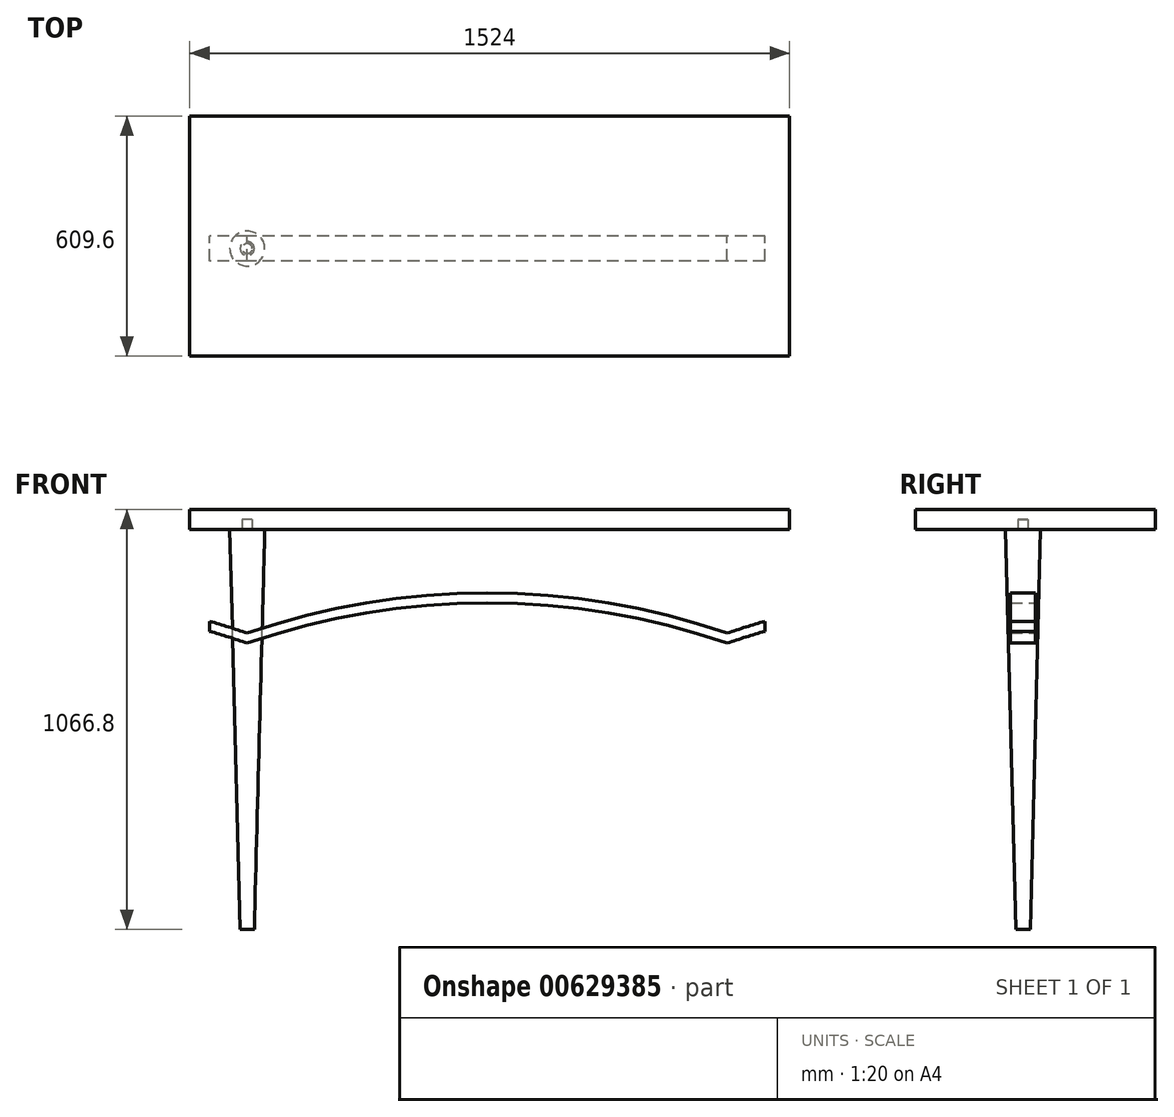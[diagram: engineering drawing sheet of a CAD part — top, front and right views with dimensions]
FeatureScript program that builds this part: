
annotation { "Feature Type Name" : "Feature", "Feature Type Description" : "" }
export const myFeature = defineFeature(function(context is Context, id is Id, definition is map)
    precondition{}
    {
        {
            var Q0;
            Q0=qCreatedBy(makeId("Top.planeOp"),FACE);
            var sketch = newSketch(context, id + "F0", { "sketchPlane" : qUnion([Q0])});
            skLineSegment(sketch, "E0.bottom", {"start": v(762, -304.8) * mm, "end": v(-762, -304.8) * mm});
            skLineSegment(sketch, "E0.top", {"start": v(762, 304.8) * mm, "end": v(-762, 304.8) * mm});
            skLineSegment(sketch, "E0.left", {"start": v(762, -304.8) * mm, "end": v(762, 304.8) * mm});
            skLineSegment(sketch, "E0.right", {"start": v(-762, -304.8) * mm, "end": v(-762, 304.8) * mm});
            skPoint(sketch, "E0.middle", {"position": v(0, 0) * mm});
            skSolve(sketch);
        }
        {
            var Q0;
            Q0 = qSketchRegion(id + "F0", true);
            extrude(context, id + "F1", {"entities" : qUnion([Q0]), "depth" : 50.8 * mm, "offsetDistance" : 25.4 * mm});
        }
        {
            var Q0;
            Q0=qCreatedBy(makeId("Front.planeOp"),FACE);
            var sketch = newSketch(context, id + "F2", { "sketchPlane" : qUnion([Q0])});
            skArc(sketch, "E1", {"start": v(603.21, -288.66) * mm, "mid": v(-6.39, -186.66) * mm, "end": v(-615.99, -288.66) * mm});
            skArc(sketch, "E2", {"start": v(603.21, -263.26) * mm, "mid": v(-6.39, -161.26) * mm, "end": v(-615.99, -263.26) * mm});
            skArc(sketch, "E3.MirrorCS", {"start": v(-711.57, -233.19) * mm, "mid": v(-663.58, -247.59) * mm, "end": v(-615.99, -263.26) * mm});
            skArc(sketch, "E4.MirrorCS", {"start": v(-711.57, -258.59) * mm, "mid": v(-663.58, -272.99) * mm, "end": v(-615.99, -288.66) * mm});
            skArc(sketch, "E5.MirrorCS", {"start": v(603.21, -263.26) * mm, "mid": v(650.8, -247.59) * mm, "end": v(698.8, -233.19) * mm});
            skArc(sketch, "E6.MirrorCS", {"start": v(603.21, -288.66) * mm, "mid": v(650.8, -272.99) * mm, "end": v(698.8, -258.59) * mm});
            skLineSegment(sketch, "E7", {"start": v(-711.57, -233.19) * mm, "end": v(-711.57, -258.59) * mm});
            skPoint(sketch, "E8.endSnap0", {"position": v(-6.39, -161.26) * mm});
            skLineSegment(sketch, "E9.MirrorCS", {"start": v(698.8, -233.19) * mm, "end": v(698.8, -258.59) * mm});
            skPoint(sketch, "E10.orphan", {"position": v(-1835.19, -263.26) * mm});
            skPoint(sketch, "E11.orphan", {"position": v(-1835.19, -288.66) * mm});
            skPoint(sketch, "E12.orphan", {"position": v(1822.41, -263.26) * mm});
            skPoint(sketch, "E13.orphan", {"position": v(1822.41, -288.66) * mm});
            skSolve(sketch);
        }
        {
            var Q0;
            Q0=makeQuery(id+"F2.imprint","IMPRINT",FACE,{"disambiguationData":[TD([[makeQuery(id+"F2.imprint","IMPRINT",EDGE,{"derivedFrom":sQuery(id+"F2.wireOp",EDGE,"E1")}),-1.0]])]});
            extrude(context, id + "F3", {"entities" : qUnion([Q0]), "depth" : 63.5 * mm, "offsetDistance" : 25.4 * mm});
        }
        {
            var Q0;
            Q0=qCreatedBy(makeId("Top.planeOp"),FACE);
            var sketch = newSketch(context, id + "F4", { "sketchPlane" : qUnion([Q0])});
            skLineSegment(sketch, "E14.0", {"start": v(-615.99, -63.5) * mm, "end": v(-615.99, 0) * mm, "construction": true});
            skCircle(sketch, "E15", {"center": v(-615.99, -31.75) * mm, "radius": 44.45 * mm});
            skSolve(sketch);
        }
        {
            var Q0;
            Q0=makeQuery(id+"F4.imprint","IMPRINT",FACE,{"disambiguationData":[TD([[makeQuery(id+"F4.imprint","IMPRINT",EDGE,{"derivedFrom":sQuery(id+"F4.wireOp",EDGE,"E15")}),1.0]])]});
            extrude(context, id + "F5", {"entities" : qUnion([Q0]), "oppositeDirection" : true, "depth" : 1016 * mm, "offsetDistance" : 25.4 * mm, "hasDraft" : true, "draftAngle" : 1.5 * degree, "draftPullDirection" : true});
        }
        {
            var Q0;
            Q0=qCreatedBy(makeId("Top.planeOp"),FACE);
            var sketch = newSketch(context, id + "F6", { "sketchPlane" : qUnion([Q0])});
            skCircle(sketch, "E16.0", {"center": v(-615.99, -31.75) * mm, "radius": 44.45 * mm, "construction": true});
            skCircle(sketch, "E17", {"center": v(-615.99, -31.75) * mm, "radius": 12.7 * mm});
            skSolve(sketch);
        }
        {
            var Q0;
            Q0=makeQuery(id+"F6.imprint","IMPRINT",FACE,{"disambiguationData":[TD([[makeQuery(id+"F6.imprint","IMPRINT",EDGE,{"derivedFrom":sQuery(id+"F6.wireOp",EDGE,"E17")}),1.0]])]});
            extrude(context, id + "F7", {"entities" : qUnion([Q0]), "depth" : 25.4 * mm, "offsetDistance" : 25.4 * mm});
        }
    });
